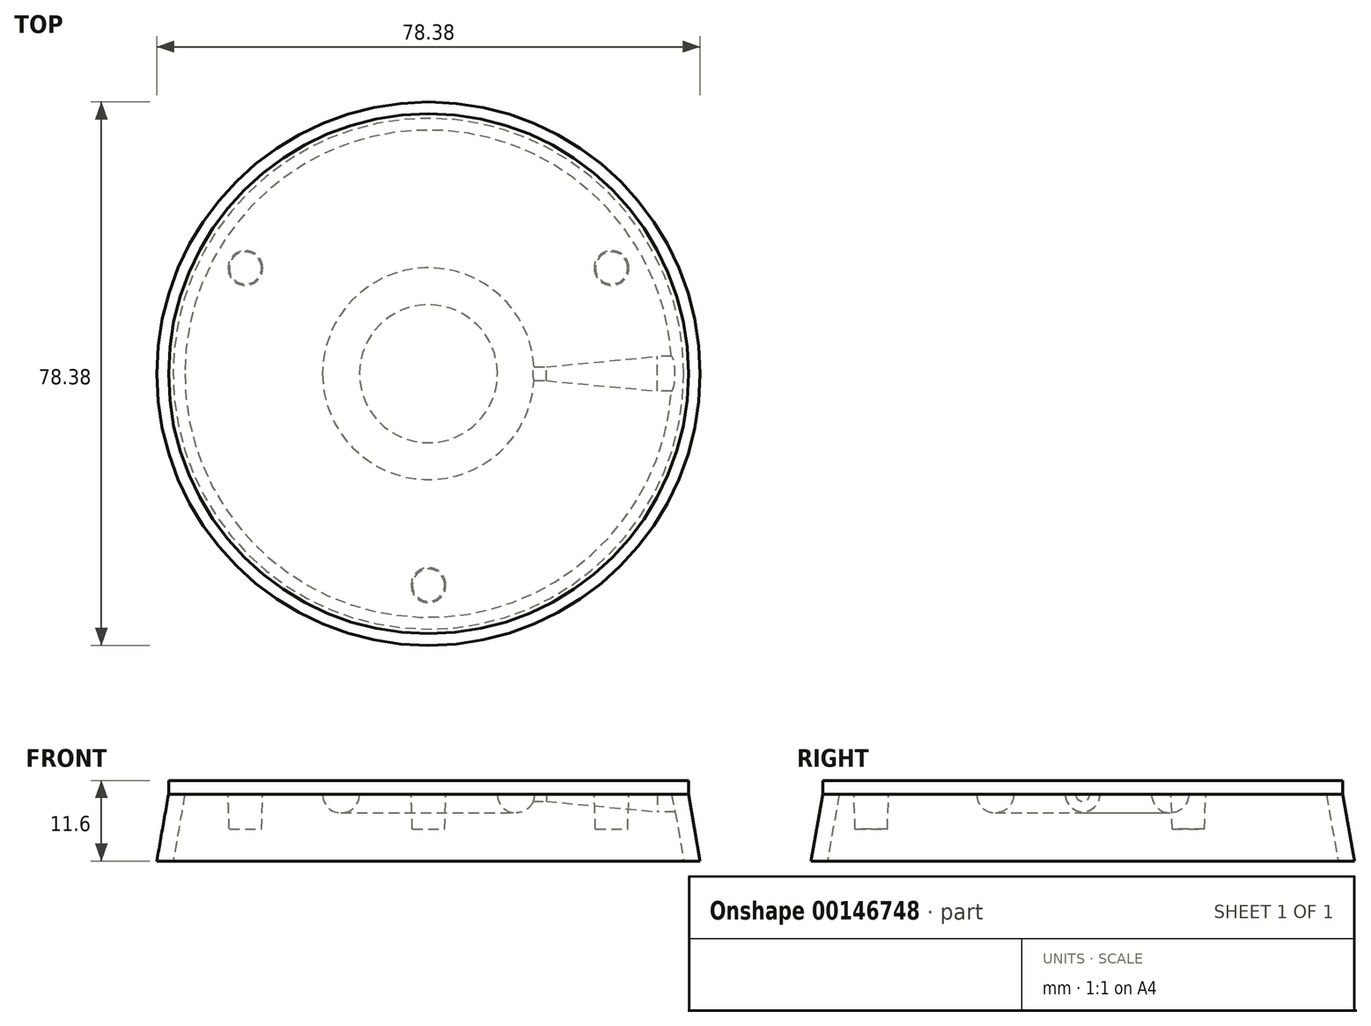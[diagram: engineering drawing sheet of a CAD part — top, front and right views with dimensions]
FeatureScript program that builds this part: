
annotation { "Feature Type Name" : "Feature", "Feature Type Description" : "" }
export const myFeature = defineFeature(function(context is Context, id is Id, definition is map)
    precondition{}
    {
        {
            var Q0;
            Q0=qCreatedBy(makeId("Front.planeOp"),FACE);
            var sketch = newSketch(context, id + "F0", { "sketchPlane" : qUnion([Q0])});
            skLineSegment(sketch, "E0", {"start": v(0, 0) * mm, "end": v(0, 36.8) * mm, "construction": true});
            skSolve(sketch);
        }
        {
            var Q0;
            Q0=qCreatedBy(makeId("Front.planeOp"),FACE);
            var sketch = newSketch(context, id + "F1", { "sketchPlane" : qUnion([Q0])});
            skLineSegment(sketch, "E1", {"start": v(-15.28, 0) * mm, "end": v(-9.95, 0) * mm});
            skArc(sketch, "E2", {"start": v(-15.28, 0) * mm, "mid": v(-12.61, -2.67) * mm, "end": v(-9.95, 0) * mm});
            skSolve(sketch);
        }
        {
            var Q0;
            Q0=qSketchRegion(id+"F1",true);
            var Q1;
            Q1=sQuery(id+"F0.wireOp",EDGE,"E0");
            revolve(context, id + "F2", {"entities" : qUnion([Q0]), "axis" : qUnion([Q1]), "revolveType" : RevolveType.FULL});
        }
        {
            var Q0;
            Q0=makeQuery(id+"F2.opRevolve","SWEPT_FACE",FACE,{"disambiguationData":[OSD([sQuery(id+"F1.wireOp",EDGE,"E1")])]});
            var sketch = newSketch(context, id + "F3", { "sketchPlane" : qUnion([Q0])});
            skCircle(sketch, "E3", {"center": v(0, 0) * mm, "radius": 37.5 * mm});
            skSolve(sketch);
        }
        {
            var Q0;
            Q0=qSketchRegion(id+"F3",true);
            extrude(context, id + "F4", {"entities" : qUnion([Q0]), "operationType" : NewBodyOperationType.ADD, "depth" : 2 * mm});
        }
        {
            var Q0;
            Q0=qCreatedBy(makeId("Right.planeOp"),FACE);
            var sketch = newSketch(context, id + "F5", { "sketchPlane" : qUnion([Q0])});
            skLineSegment(sketch, "E4", {"start": v(-35.14, 0) * mm, "end": v(-37.5, 0) * mm});
            skLineSegment(sketch, "E5", {"start": v(-37.5, 0) * mm, "end": v(-39.2, -9.6) * mm});
            skLineSegment(sketch, "E6", {"start": v(-39.2, -9.6) * mm, "end": v(-36.84, -9.6) * mm});
            skLineSegment(sketch, "E7", {"start": v(-36.84, -9.6) * mm, "end": v(-35.14, 0) * mm});
            skSolve(sketch);
        }
        {
            var Q0;
            Q0=qSketchRegion(id+"F5",true);
            var Q1;
            Q1=sQuery(id+"F0.wireOp",EDGE,"E0");
            revolve(context, id + "F6", {"operationType" : NewBodyOperationType.ADD, "entities" : qUnion([Q0]), "axis" : qUnion([Q1]), "revolveType" : RevolveType.FULL});
        }
        {
            var Q0;
            {var subQ0=sQuery(id+"F3.wireOp",EDGE,"E3");Q0=makeQuery(id+"F4.boolean.opBoolean","SPLIT",FACE,{"disambiguationData":[TD([makeQuery(id+"F2.opRevolve","SWEPT_FACE",FACE,{"disambiguationData":[OSD([sQuery(id+"F1.wireOp",EDGE,"E2")])]}),makeQuery(id+"F4.opExtrude","SWEPT_FACE",FACE,{"disambiguationData":[OSD([subQ0])]})])],"derivedFrom":makeQuery(id+"F4.opExtrude","CAP_FACE",FACE,{"disambiguationData":[OSD([subQ0])],"isStart":true})});}
            var sketch = newSketch(context, id + "F7", { "sketchPlane" : qUnion([Q0])});
            skCircle(sketch, "E8", {"center": v(0, 0) * mm, "radius": 30.5 * mm, "construction": true});
            skCircle(sketch, "E9", {"center": v(0, 30.5) * mm, "radius": 2.5 * mm});
            skCircle(sketch, "E10.1.0", {"center": v(-26.41, -15.25) * mm, "radius": 2.5 * mm});
            skCircle(sketch, "E10.2.0", {"center": v(26.41, -15.25) * mm, "radius": 2.5 * mm});
            skSolve(sketch);
        }
        {
            var Q0;
            Q0=qSketchRegion(id+"F7",true);
            extrude(context, id + "F8", {"entities" : qUnion([Q0]), "operationType" : NewBodyOperationType.ADD, "depth" : 5 * mm, "hasDraft" : true, "draftAngle" : 2 * degree, "draftPullDirection" : true});
        }
        {
            var Q0;
            Q0=qCreatedBy(makeId("Right.planeOp"),FACE);
            cPlane(context, id + "F9", {"entities" : qUnion([Q0]), "cplaneType" : CPlaneType.OFFSET, "offset" : 33 * mm, "width" : 150 * mm, "height" : 150 * mm});
        }
        {
            var Q0;
            Q0=qCreatedBy(makeId("Right.planeOp"),FACE);
            cPlane(context, id + "F10", {"entities" : qUnion([Q0]), "cplaneType" : CPlaneType.OFFSET, "offset" : 17 * mm, "width" : 150 * mm, "height" : 150 * mm});
        }
        {
            var Q0;
            Q0=qCreatedBy(id+"F9.planeOp",FACE);
            var sketch = newSketch(context, id + "F11", { "sketchPlane" : qUnion([Q0])});
            skArc(sketch, "E11", {"start": v(-2.5, 0) * mm, "mid": v(0, -2.5) * mm, "end": v(2.5, 0) * mm});
            skLineSegment(sketch, "E12", {"start": v(-2.5, 0) * mm, "end": v(2.5, 0) * mm});
            skSolve(sketch);
        }
        {
            var Q0;
            Q0=qSketchRegion(id+"F11",true);
            var Q1;
            Q1=makeQuery(id+"F6.opRevolve","SWEPT_FACE",FACE,{"disambiguationData":[OSD([sQuery(id+"F5.wireOp",EDGE,"E7")])]});
            extrude(context, id + "F12", {"entities" : qUnion([Q0]), "operationType" : NewBodyOperationType.ADD, "endBound" : BoundingType.UP_TO_SURFACE, "endBoundEntityFace" : qUnion([Q1]), "depth" : 25 * mm});
        }
        {
            var Q0;
            Q0=qCreatedBy(id+"F10.planeOp",FACE);
            var sketch = newSketch(context, id + "F13", { "sketchPlane" : qUnion([Q0])});
            skArc(sketch, "E13", {"start": v(-1, 0) * mm, "mid": v(0, -1) * mm, "end": v(1, 0) * mm});
            skLineSegment(sketch, "E14", {"start": v(-1, 0) * mm, "end": v(1, 0) * mm});
            skSolve(sketch);
        }
        {
            var Q0;
            Q0=qSketchRegion(id+"F13",true);
            var Q1;
            Q1=makeQuery(id+"F2.opRevolve","SWEPT_FACE",FACE,{"disambiguationData":[OSD([sQuery(id+"F1.wireOp",EDGE,"E2")])]});
            extrude(context, id + "F14", {"entities" : qUnion([Q0]), "operationType" : NewBodyOperationType.ADD, "endBound" : BoundingType.UP_TO_SURFACE, "oppositeDirection" : true, "endBoundEntityFace" : qUnion([Q1]), "depth" : 25 * mm});
        }
        {
            var Q1;
            Q1=makeQuery(id+"F14.opExtrude","CAP_FACE",FACE,{"disambiguationData":[OSD([sQuery(id+"F13.wireOp",EDGE,"E13"),sQuery(id+"F13.wireOp",EDGE,"E14")])],"isStart":true});
            var Q2;
            Q2=makeQuery(id+"F12.opExtrude","CAP_FACE",FACE,{"disambiguationData":[OSD([sQuery(id+"F11.wireOp",EDGE,"E11"),sQuery(id+"F11.wireOp",EDGE,"E12")])],"isStart":true});
            loft(context, id + "F15", {"operationType" : NewBodyOperationType.ADD, "sheetProfilesArray" : [{ "sheetProfileEntities" : qUnion([Q1]) }, { "sheetProfileEntities" : qUnion([Q2]) }]});
        }
    });
